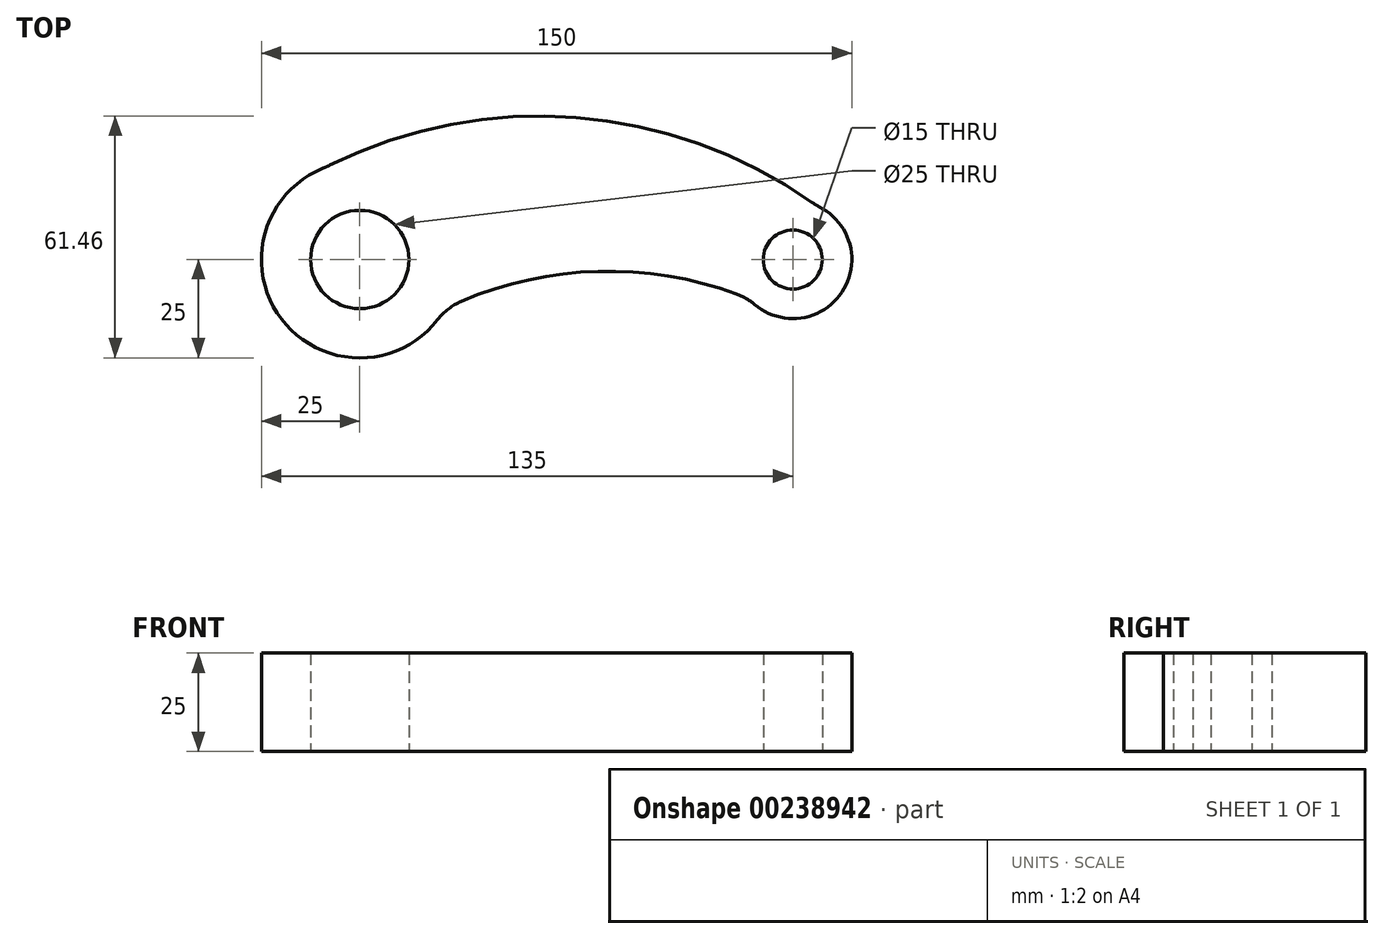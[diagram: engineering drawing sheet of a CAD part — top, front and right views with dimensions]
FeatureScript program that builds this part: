
annotation { "Feature Type Name" : "Feature", "Feature Type Description" : "" }
export const myFeature = defineFeature(function(context is Context, id is Id, definition is map)
    precondition{}
    {
        {
            var Q0;
            Q0=qCreatedBy(makeId("Top.planeOp"),FACE);
            var sketch = newSketch(context, id + "F0", { "sketchPlane" : qUnion([Q0])});
            skCircle(sketch, "E0", {"center": v(0, 0) * mm, "radius": 12.5 * mm});
            skLineSegment(sketch, "E1", {"start": v(0, 0) * mm, "end": v(110, 0) * mm});
            skCircle(sketch, "E2", {"center": v(110, 0) * mm, "radius": 7.5 * mm});
            skArc(sketch, "E3", {"start": v(-9.37, 23.18) * mm, "mid": v(-19.92, -15.11) * mm, "end": v(19.8, -15.26) * mm});
            skArc(sketch, "E4", {"start": v(100.27, -11.41) * mm, "mid": v(122.49, -8.3) * mm, "end": v(116.76, 13.39) * mm});
            skArc(sketch, "E5", {"start": v(114.88, 14.52) * mm, "mid": v(54.93, 36.1) * mm, "end": v(-7.63, 23.96) * mm});
            skArc(sketch, "E6", {"start": v(95.67, -8.73) * mm, "mid": v(60.55, -3.02) * mm, "end": v(25.78, -10.63) * mm});
            skPoint(sketch, "E7.visualSharp", {"position": v(21.64, -12.52) * mm});
            skArc(sketch, "E7.filletArc", {"start": v(25.78, -10.63) * mm, "mid": v(22.5, -12.56) * mm, "end": v(19.8, -15.26) * mm});
            skPoint(sketch, "E8.visualSharp", {"position": v(98.74, -9.92) * mm});
            skArc(sketch, "E8.filletArc", {"start": v(100.27, -11.41) * mm, "mid": v(98.09, -9.87) * mm, "end": v(95.67, -8.73) * mm});
            skPoint(sketch, "E9.visualSharp", {"position": v(-8.59, 23.48) * mm});
            skArc(sketch, "E9.filletArc", {"start": v(-9.37, 23.18) * mm, "mid": v(-8.5, 23.55) * mm, "end": v(-7.63, 23.96) * mm});
            skPoint(sketch, "E10.visualSharp", {"position": v(115.9, 13.79) * mm});
            skArc(sketch, "E10.filletArc", {"start": v(114.88, 14.52) * mm, "mid": v(115.8, 13.92) * mm, "end": v(116.76, 13.39) * mm});
            skSolve(sketch);
        }
        {
            var Q0;
            Q0 = qSketchRegion(id + "F0", true);
            extrude(context, id + "F1", {"entities" : qUnion([Q0]), "depth" : 25 * mm});
        }
    });
